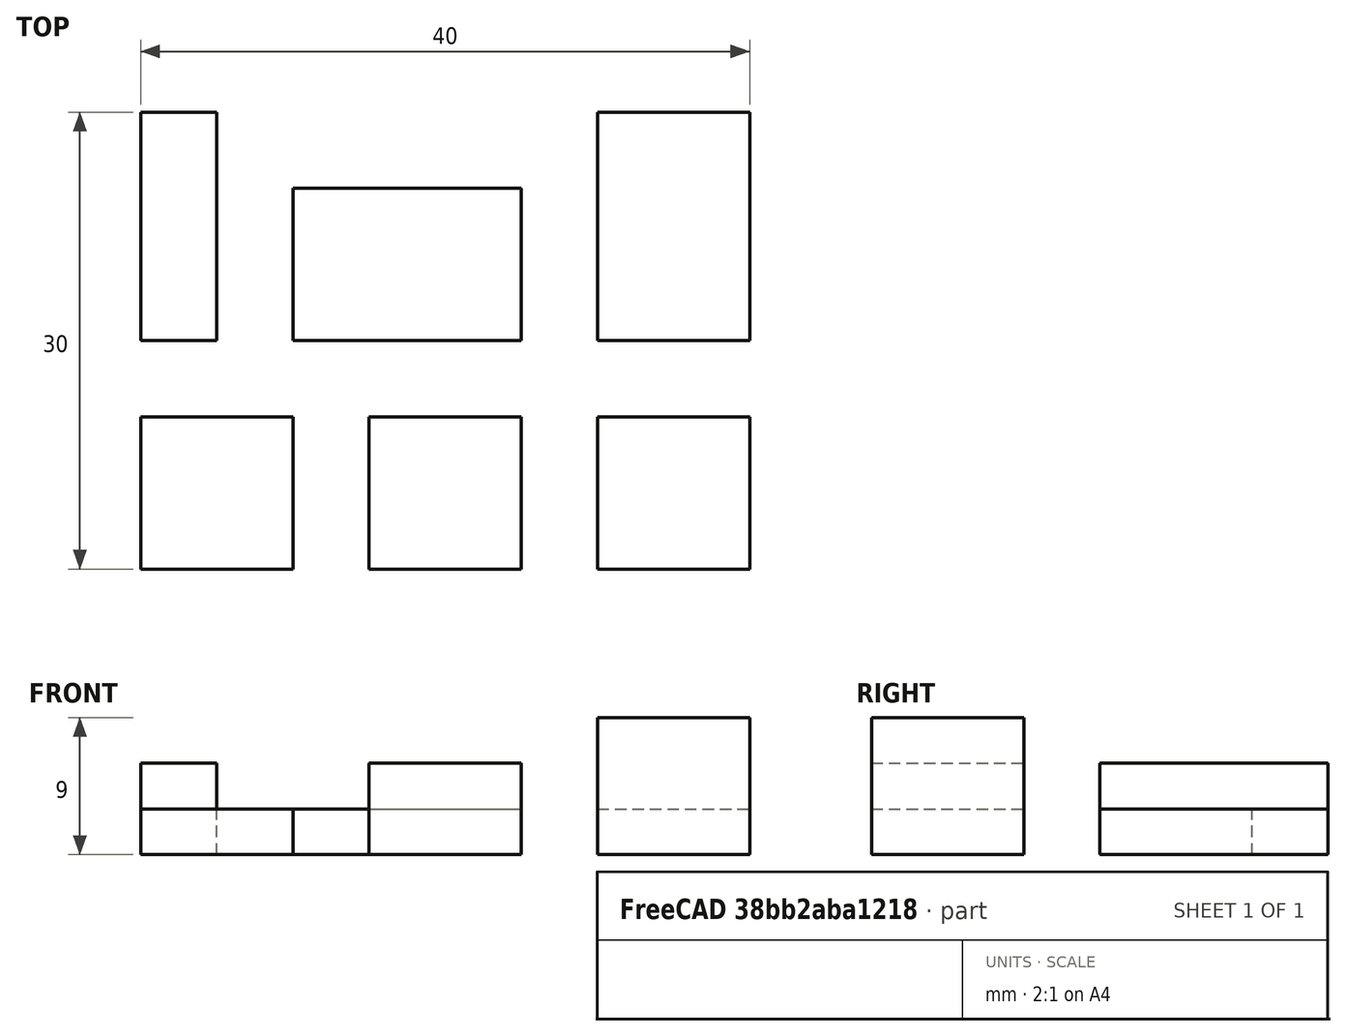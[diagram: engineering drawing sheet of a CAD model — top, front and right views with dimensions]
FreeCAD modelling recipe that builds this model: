
FCSTD DOCUMENT  (FreeCAD 0.16R6703 (Git))
Label: quads-test
License: All rights reserved
LicenseURL: http://en.wikipedia.org/wiki/All_rights_reserved
objects: Part::Box×6
note: 6 computed .brp shape members not serialized (recipe doc carries the construction recipe); baked Part::Feature solids carry a one-line shape summary decoded from their .brp

FEATURE [Part::Box] Box  label="Cube"
  Height = 3
  Length = 10
  Width = 10
FEATURE [Part::Box] Box001  label="Cube001"
  Height = 6
  Length = 10
  Placement = pos=(15,0,0) rot=(0,0,1;0rad)
  Width = 10
FEATURE [Part::Box] Box002  label="Cube002"
  Height = 9
  Length = 10
  Placement = pos=(30,0,0) rot=(0,0,1;0rad)
  Width = 10
FEATURE [Part::Box] Box003  label="Cube003"
  Height = 3
  Length = 10
  Placement = pos=(30,15,0) rot=(0,0,1;0rad)
  Width = 15
FEATURE [Part::Box] Box004  label="Cube004"
  Height = 3
  Length = 15
  Placement = pos=(10,15,0) rot=(0,0,1;0rad)
  Width = 10
FEATURE [Part::Box] Box005  label="Cube005"
  Height = 6
  Length = 5
  Placement = pos=(0,15,0) rot=(0,0,1;0rad)
  Width = 15
